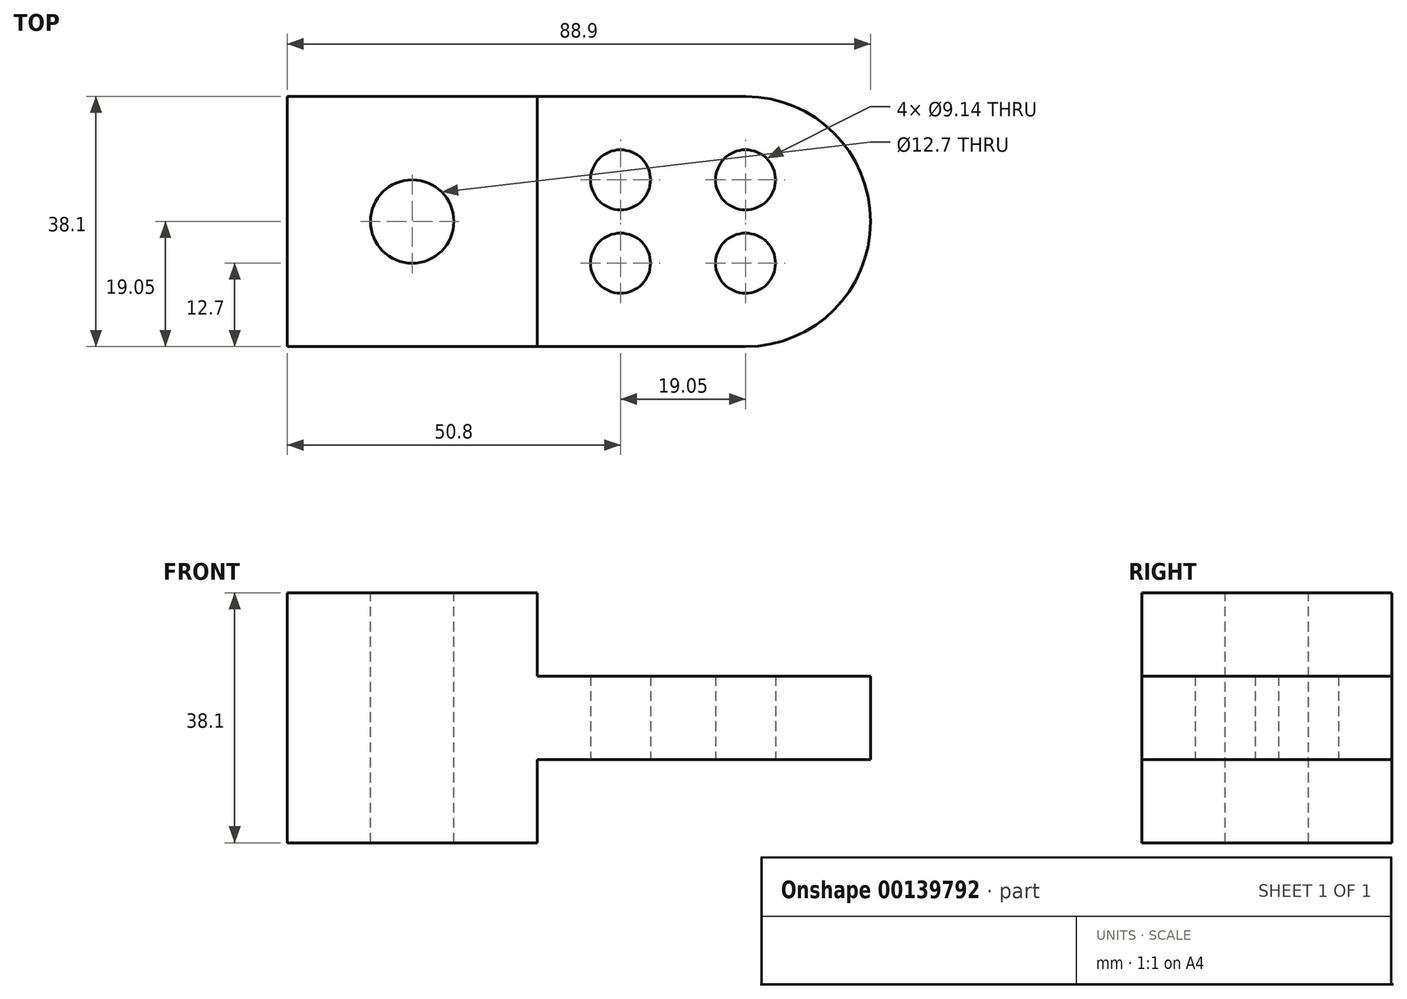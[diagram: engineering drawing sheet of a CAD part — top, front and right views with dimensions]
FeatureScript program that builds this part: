
annotation { "Feature Type Name" : "Feature", "Feature Type Description" : "" }
export const myFeature = defineFeature(function(context is Context, id is Id, definition is map)
    precondition{}
    {
        {
            var Q0;
            Q0=qCreatedBy(makeId("Top.planeOp"),FACE);
            var sketch = newSketch(context, id + "F0", { "sketchPlane" : qUnion([Q0])});
            skLineSegment(sketch, "E0.bottom", {"start": v(-19.05, -19.05) * mm, "end": v(19.05, -19.05) * mm});
            skLineSegment(sketch, "E0.top", {"start": v(-19.05, 19.05) * mm, "end": v(19.05, 19.05) * mm});
            skLineSegment(sketch, "E0.left", {"start": v(-19.05, -19.05) * mm, "end": v(-19.05, 19.05) * mm});
            skLineSegment(sketch, "E0.right", {"start": v(19.05, -19.05) * mm, "end": v(19.05, 19.05) * mm});
            skPoint(sketch, "E0.middle", {"position": v(0, 0) * mm});
            skLineSegment(sketch, "E1", {"start": v(19.05, 19.05) * mm, "end": v(50.8, 19.05) * mm});
            skLineSegment(sketch, "E2", {"start": v(19.05, -19.05) * mm, "end": v(50.8, -19.05) * mm});
            skArc(sketch, "E3", {"start": v(50.8, -19.05) * mm, "mid": v(69.85, 0) * mm, "end": v(50.8, 19.05) * mm});
            skCircle(sketch, "E4", {"center": v(50.8, 6.35) * mm, "radius": 4.57 * mm});
            skCircle(sketch, "E5.0.1.0", {"center": v(50.8, -6.35) * mm, "radius": 4.57 * mm});
            skCircle(sketch, "E5.1.0.0", {"center": v(31.75, 6.35) * mm, "radius": 4.57 * mm});
            skCircle(sketch, "E5.1.1.0", {"center": v(31.75, -6.35) * mm, "radius": 4.57 * mm});
            skLineSegment(sketch, "E5.direction1", {"start": v(50.8, 6.35) * mm, "end": v(31.75, 6.35) * mm, "construction": true});
            skLineSegment(sketch, "E5.direction2", {"start": v(50.8, 6.35) * mm, "end": v(50.8, -6.35) * mm, "construction": true});
            skSolve(sketch);
        }
        {
            var Q0;
            Q0=makeQuery(id+"F0.imprint","IMPRINT",FACE,{"disambiguationData":[TD([[makeQuery(id+"F0.imprint","IMPRINT",EDGE,{"derivedFrom":sQuery(id+"F0.wireOp",EDGE,"E0.bottom")}),1.0]])]});
            extrude(context, id + "F1", {"entities" : qUnion([Q0]), "endBound" : BoundingType.SYMMETRIC, "depth" : 38.1 * mm});
        }
        {
            var Q0;
            Q0=makeQuery(id+"F0.imprint","IMPRINT",FACE,{"disambiguationData":[TD([[makeQuery(id+"F0.imprint","IMPRINT",EDGE,{"derivedFrom":sQuery(id+"F0.wireOp",EDGE,"E0.right")}),-1.0]])]});
            extrude(context, id + "F2", {"entities" : qUnion([Q0]), "operationType" : NewBodyOperationType.ADD, "endBound" : BoundingType.SYMMETRIC, "depth" : 12.7 * mm});
        }
        {
            var Q0;
            Q0=makeQuery(id+"F1.opExtrude","CAP_FACE",FACE,{"disambiguationData":[OSD([sQuery(id+"F0.wireOp",EDGE,"E0.bottom"),sQuery(id+"F0.wireOp",EDGE,"E0.top"),sQuery(id+"F0.wireOp",EDGE,"E0.left"),sQuery(id+"F0.wireOp",EDGE,"E0.right")])],"isStart":false});
            var sketch = newSketch(context, id + "F3", { "sketchPlane" : qUnion([Q0])});
            skCircle(sketch, "E6", {"center": v(0, 0) * mm, "radius": 6.35 * mm});
            skSolve(sketch);
        }
        {
            var Q0;
            Q0 = qSketchRegion(id + "F3", true);
            extrude(context, id + "F4", {"entities" : qUnion([Q0]), "operationType" : NewBodyOperationType.REMOVE, "endBound" : BoundingType.THROUGH_ALL, "oppositeDirection" : true, "depth" : 25.4 * mm});
        }
    });
